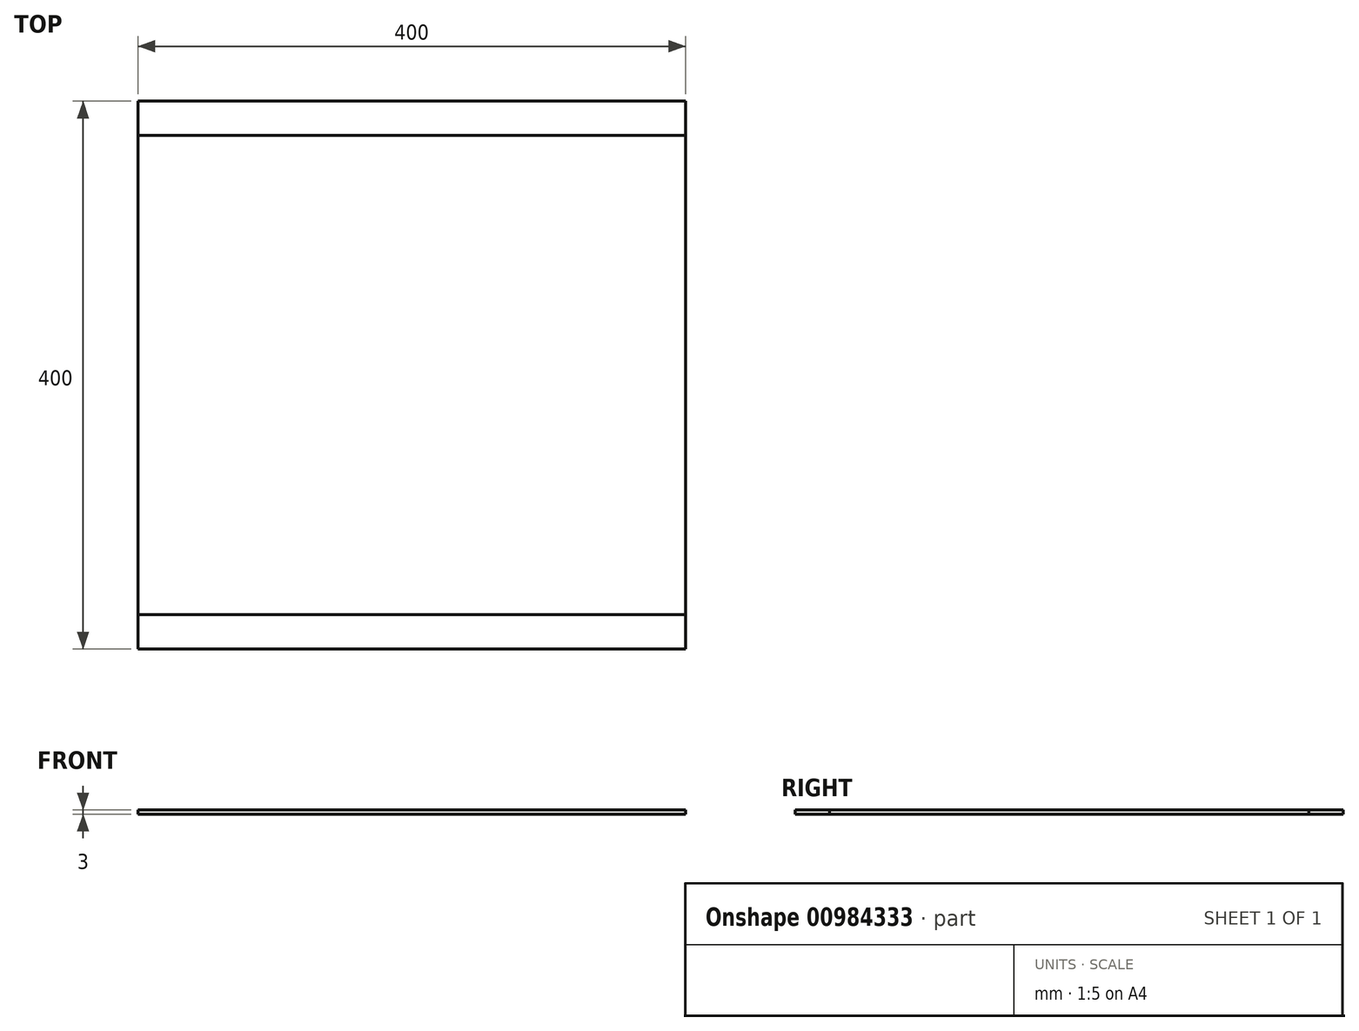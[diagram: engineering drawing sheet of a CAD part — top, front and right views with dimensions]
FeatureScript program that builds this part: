
annotation { "Feature Type Name" : "Feature", "Feature Type Description" : "" }
export const myFeature = defineFeature(function(context is Context, id is Id, definition is map)
    precondition{}
    {
        {
            var Q0;
            Q0=qCreatedBy(makeId("Top.planeOp"),FACE);
            var sketch = newSketch(context, id + "F0", { "sketchPlane" : qUnion([Q0])});
            skLineSegment(sketch, "E0.bottom", {"start": v(200, 200) * mm, "end": v(-200, 200) * mm});
            skLineSegment(sketch, "E0.top", {"start": v(200, -200) * mm, "end": v(-200, -200) * mm});
            skLineSegment(sketch, "E0.left", {"start": v(200, 200) * mm, "end": v(200, -200) * mm});
            skLineSegment(sketch, "E0.right", {"start": v(-200, 200) * mm, "end": v(-200, -200) * mm});
            skPoint(sketch, "E0.middle", {"position": v(0, 0) * mm});
            skLineSegment(sketch, "E1.bottom", {"start": v(200, 175) * mm, "end": v(-200, 175) * mm});
            skLineSegment(sketch, "E1.top", {"start": v(200, -175) * mm, "end": v(-200, -175) * mm});
            skLineSegment(sketch, "E1.left", {"start": v(200, 175) * mm, "end": v(200, -175) * mm});
            skLineSegment(sketch, "E1.right", {"start": v(-200, 175) * mm, "end": v(-200, -175) * mm});
            skSolve(sketch);
        }
        {
            var Q0;
            Q0=makeQuery(id+"F0.imprint","IMPRINT",FACE,{"disambiguationData":[TD([[makeQuery(id+"F0.imprint","IMPRINT",EDGE,{"derivedFrom":sQuery(id+"F0.wireOp",EDGE,"E1.bottom")}),1.0]])]});
            var Q1;
            {var subQ0=sQuery(id+"F0.wireOp",EDGE,"E0.bottom");Q1=makeQuery(id+"F0.imprint","IMPRINT",FACE,{"disambiguationData":[TD([[makeQuery(id+"F0.imprint","IMPRINT",EDGE,{"derivedFrom":subQ0}),1.0]])]});}
            var Q2;
            {var subQ0=sQuery(id+"F0.wireOp",EDGE,"E0.top");Q2=makeQuery(id+"F0.imprint","IMPRINT",FACE,{"disambiguationData":[TD([[makeQuery(id+"F0.imprint","IMPRINT",EDGE,{"derivedFrom":subQ0}),-1.0]])]});}
            extrude(context, id + "F1", {"entities" : qUnion([Q0, Q1, Q2]), "depth" : 3 * mm, "offsetDistance" : 25 * mm});
        }
        {
            var Q0;
            Q0=makeQuery(id+"F0.imprint","IMPRINT",FACE,{"disambiguationData":[TD([[makeQuery(id+"F0.imprint","IMPRINT",EDGE,{"derivedFrom":sQuery(id+"F0.wireOp",EDGE,"E1.bottom")}),1.0]])]});
            extrude(context, id + "F2", {"entities" : qUnion([Q0]), "depth" : 3 * mm, "offsetDistance" : 25 * mm});
        }
    });
